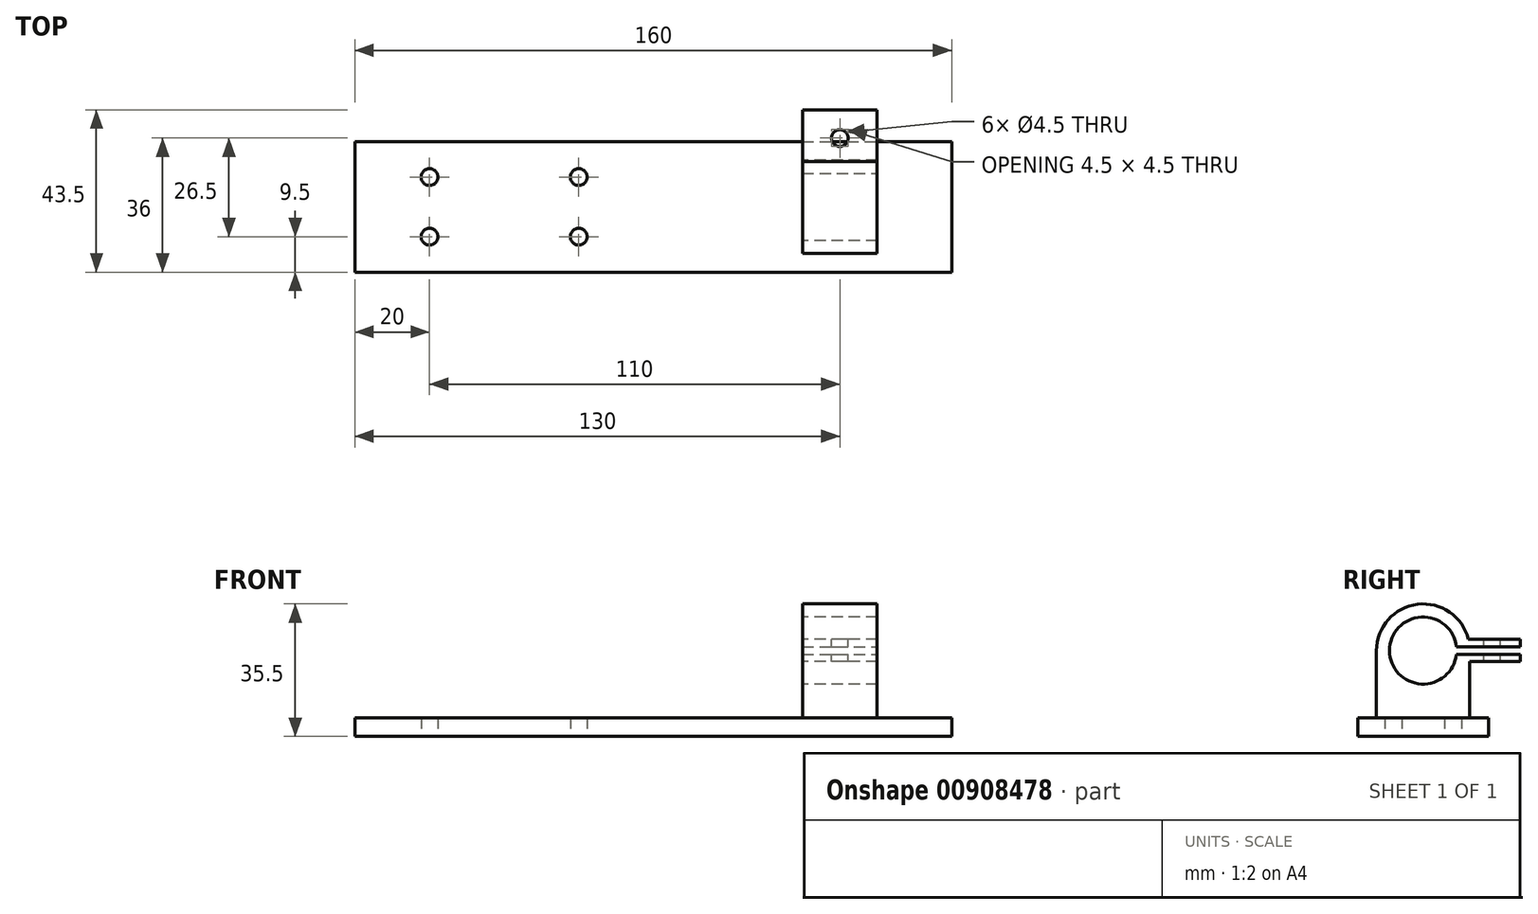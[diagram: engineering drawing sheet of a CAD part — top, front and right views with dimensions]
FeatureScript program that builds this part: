
annotation { "Feature Type Name" : "Feature", "Feature Type Description" : "" }
export const myFeature = defineFeature(function(context is Context, id is Id, definition is map)
    precondition{}
    {
        {
            var Q0;
            Q0=qCreatedBy(makeId("Top.planeOp"),FACE);
            var sketch = newSketch(context, id + "F0", { "sketchPlane" : qUnion([Q0])});
            skLineSegment(sketch, "E0.bottom", {"start": v(0, 0) * mm, "end": v(160, 0) * mm});
            skLineSegment(sketch, "E0.top", {"start": v(0, 35) * mm, "end": v(160, 35) * mm});
            skLineSegment(sketch, "E0.left", {"start": v(0, 0) * mm, "end": v(0, 35) * mm});
            skLineSegment(sketch, "E0.right", {"start": v(160, 0) * mm, "end": v(160, 35) * mm});
            skSolve(sketch);
        }
        {
            var Q0;
            Q0=makeQuery(id+"F0.imprint","IMPRINT",FACE,{"disambiguationData":[TD([[makeQuery(id+"F0.imprint","IMPRINT",EDGE,{"derivedFrom":sQuery(id+"F0.wireOp",EDGE,"E0.bottom")}),1.0]])]});
            extrude(context, id + "F1", {"entities" : qUnion([Q0]), "depth" : 5 * mm, "offsetDistance" : 25 * mm});
        }
        {
            var Q0;
            Q0=makeQuery(id+"F1.opExtrude","CAP_FACE",FACE,{"disambiguationData":[OSD([sQuery(id+"F0.wireOp",EDGE,"E0.bottom"),sQuery(id+"F0.wireOp",EDGE,"E0.top"),sQuery(id+"F0.wireOp",EDGE,"E0.left"),sQuery(id+"F0.wireOp",EDGE,"E0.right")])],"isStart":true});
            var sketch = newSketch(context, id + "F2", { "sketchPlane" : qUnion([Q0])});
            skCircle(sketch, "E1", {"center": v(20, -9.5) * mm, "radius": 2.25 * mm});
            skCircle(sketch, "E2", {"center": v(20, -25.5) * mm, "radius": 2.25 * mm});
            skCircle(sketch, "E3", {"center": v(60, -9.5) * mm, "radius": 2.25 * mm});
            skCircle(sketch, "E4", {"center": v(60, -25.5) * mm, "radius": 2.25 * mm});
            skSolve(sketch);
        }
        {
            var Q0;
            Q0=sQuery(id+"F2.wireOp",VERTEX,"E1.center");
            var Q1;
            Q1=sQuery(id+"F2.wireOp",VERTEX,"E3.center");
            var Q2;
            Q2=sQuery(id+"F2.wireOp",VERTEX,"E4.center");
            var Q3;
            Q3=sQuery(id+"F2.wireOp",VERTEX,"E2.center");
            var Q4;
            Q4=makeQuery(id+"F1.opExtrude","SWEPT_BODY",BODY,{"disambiguationData":[OSD([sQuery(id+"F0.wireOp",EDGE,"E0.bottom"),sQuery(id+"F0.wireOp",EDGE,"E0.top"),sQuery(id+"F0.wireOp",EDGE,"E0.left"),sQuery(id+"F0.wireOp",EDGE,"E0.right")])]});
            hole(context, id + "F3", {"style" : HoleStyle.SIMPLE, "endStyle" : HoleEndStyle.THROUGH, "standardTappedOrClearance" : lookupTablePath({ "fit" : "Normal", "standard" : "ISO", "size" : "M4", "type" : "Clearance" }), "standardBlindInLast" : lookupTablePath({ "fit" : "Normal", "standard" : "ISO", "size" : "M4", "type" : "Clearance" }), "holeDiameter" : 4.5 * mm, "majorDiameter" : 5 * mm, "isTappedThrough" : true, "tappedDepth" : 12 * mm, "tapClearance" : 3, "locations" : qUnion([Q0, Q1, Q2, Q3]), "scope" : qUnion([Q4])});
        }
        {
            var Q0;
            Q0=qCreatedBy(makeId("Right.planeOp"),FACE);
            cPlane(context, id + "F4", {"entities" : qUnion([Q0]), "cplaneType" : CPlaneType.OFFSET, "offset" : 120 * mm, "width" : 150 * mm, "height" : 150 * mm});
        }
        {
            var Q0;
            Q0=qCreatedBy(id+"F4.planeOp",FACE);
            var sketch = newSketch(context, id + "F5", { "sketchPlane" : qUnion([Q0])});
            skLineSegment(sketch, "E5", {"start": v(5, 5) * mm, "end": v(30, 5) * mm});
            skLineSegment(sketch, "E6", {"start": v(5, 5) * mm, "end": v(5, 23) * mm});
            skLineSegment(sketch, "E7", {"start": v(30, 5) * mm, "end": v(30, 23) * mm});
            skArc(sketch, "E8", {"start": v(30, 23) * mm, "mid": v(17.5, 35.5) * mm, "end": v(5, 23) * mm});
            skCircle(sketch, "E9", {"center": v(17.5, 23) * mm, "radius": 9 * mm});
            skSolve(sketch);
        }
        {
            var Q0;
            Q0=makeQuery(id+"F5.imprint","IMPRINT",FACE,{"disambiguationData":[TD([[makeQuery(id+"F5.imprint","IMPRINT",EDGE,{"derivedFrom":sQuery(id+"F5.wireOp",EDGE,"E5")}),1.0]])]});
            extrude(context, id + "F6", {"entities" : qUnion([Q0]), "operationType" : NewBodyOperationType.ADD, "depth" : 20 * mm, "offsetDistance" : 25 * mm});
        }
        {
            var Q0;
            Q0=makeQuery(id+"F6.opExtrude","CAP_FACE",FACE,{"disambiguationData":[OSD([sQuery(id+"F5.wireOp",EDGE,"E5"),sQuery(id+"F5.wireOp",EDGE,"E6"),sQuery(id+"F5.wireOp",EDGE,"E7"),sQuery(id+"F5.wireOp",EDGE,"E8"),sQuery(id+"F5.wireOp",EDGE,"E9")])],"isStart":false});
            var sketch = newSketch(context, id + "F7", { "sketchPlane" : qUnion([Q0])});
            skLineSegment(sketch, "E10", {"start": v(26.44, 24) * mm, "end": v(29.96, 24) * mm});
            skLineSegment(sketch, "E11", {"start": v(26.44, 22) * mm, "end": v(30, 22) * mm});
            skArc(sketch, "E12", {"start": v(26.44, 22) * mm, "mid": v(26.5, 23) * mm, "end": v(26.44, 24) * mm});
            skLineSegment(sketch, "E13", {"start": v(30, 22) * mm, "end": v(30, 23) * mm});
            skArc(sketch, "E14", {"start": v(30, 23) * mm, "mid": v(29.99, 23.5) * mm, "end": v(29.96, 24) * mm});
            skSolve(sketch);
        }
        {
            var Q0;
            Q0=makeQuery(id+"F7.imprint","IMPRINT",FACE,{"disambiguationData":[TD([[makeQuery(id+"F7.imprint","IMPRINT",EDGE,{"derivedFrom":sQuery(id+"F7.wireOp",EDGE,"E10")}),-1.0]])]});
            extrude(context, id + "F8", {"entities" : qUnion([Q0]), "operationType" : NewBodyOperationType.REMOVE, "oppositeDirection" : true, "depth" : 25 * mm, "offsetDistance" : 25 * mm});
        }
        {
            var Q0;
            Q0=qCreatedBy(id+"F4.planeOp",FACE);
            var sketch = newSketch(context, id + "F9", { "sketchPlane" : qUnion([Q0])});
            skLineSegment(sketch, "E15.bottom", {"start": v(28.5, 24) * mm, "end": v(43.5, 24) * mm});
            skLineSegment(sketch, "E15.top", {"start": v(28.5, 26) * mm, "end": v(43.5, 26) * mm});
            skLineSegment(sketch, "E15.left", {"start": v(28.5, 24) * mm, "end": v(28.5, 26) * mm});
            skLineSegment(sketch, "E15.right", {"start": v(43.5, 24) * mm, "end": v(43.5, 26) * mm});
            skLineSegment(sketch, "E16.bottom", {"start": v(28.5, 22) * mm, "end": v(43.5, 22) * mm});
            skLineSegment(sketch, "E16.top", {"start": v(28.5, 20) * mm, "end": v(43.5, 20) * mm});
            skLineSegment(sketch, "E16.left", {"start": v(28.5, 22) * mm, "end": v(28.5, 20) * mm});
            skLineSegment(sketch, "E16.right", {"start": v(43.5, 22) * mm, "end": v(43.5, 20) * mm});
            skSolve(sketch);
        }
        {
            var Q0;
            Q0=makeQuery(id+"F9.imprint","IMPRINT",FACE,{"disambiguationData":[TD([[makeQuery(id+"F9.imprint","IMPRINT",EDGE,{"derivedFrom":sQuery(id+"F9.wireOp",EDGE,"E16.bottom")}),-1.0]])]});
            var Q1;
            Q1=makeQuery(id+"F9.imprint","IMPRINT",FACE,{"disambiguationData":[TD([[makeQuery(id+"F9.imprint","IMPRINT",EDGE,{"derivedFrom":sQuery(id+"F9.wireOp",EDGE,"E15.bottom")}),1.0]])]});
            extrude(context, id + "F10", {"entities" : qUnion([Q0, Q1]), "operationType" : NewBodyOperationType.ADD, "depth" : 20 * mm, "offsetDistance" : 25 * mm});
        }
        {
            var Q0;
            Q0=makeQuery(id+"F10.opExtrude","SWEPT_FACE",FACE,{"disambiguationData":[OSD([sQuery(id+"F9.wireOp",EDGE,"E15.top")])]});
            var sketch = newSketch(context, id + "F11", { "sketchPlane" : qUnion([Q0])});
            skCircle(sketch, "E17", {"center": v(130, 36) * mm, "radius": 2.5 * mm, "construction": true});
            skLineSegment(sketch, "E18", {"start": v(130, 36) * mm, "end": v(120, 36) * mm, "construction": true});
            skSolve(sketch);
        }
        {
            var Q0;
            Q0=sQuery(id+"F11.wireOp",VERTEX,"E18.start");
            var Q1;
            Q1=makeQuery(id+"F1.opExtrude","SWEPT_BODY",BODY,{"disambiguationData":[OSD([sQuery(id+"F0.wireOp",EDGE,"E0.bottom"),sQuery(id+"F0.wireOp",EDGE,"E0.top"),sQuery(id+"F0.wireOp",EDGE,"E0.left"),sQuery(id+"F0.wireOp",EDGE,"E0.right")])]});
            hole(context, id + "F12", {"style" : HoleStyle.SIMPLE, "endStyle" : HoleEndStyle.BLIND, "standardTappedOrClearance" : lookupTablePath({ "fit" : "Normal", "standard" : "ISO", "size" : "M4", "type" : "Clearance" }), "standardBlindInLast" : lookupTablePath({ "fit" : "Normal", "standard" : "ISO", "size" : "M4", "type" : "Clearance" }), "holeDiameter" : 4.5 * mm, "majorDiameter" : 5 * mm, "holeDepth" : 12 * mm, "isTappedThrough" : true, "tappedDepth" : 12 * mm, "tapClearance" : 3, "locations" : qUnion([Q0]), "scope" : qUnion([Q1])});
        }
    });
